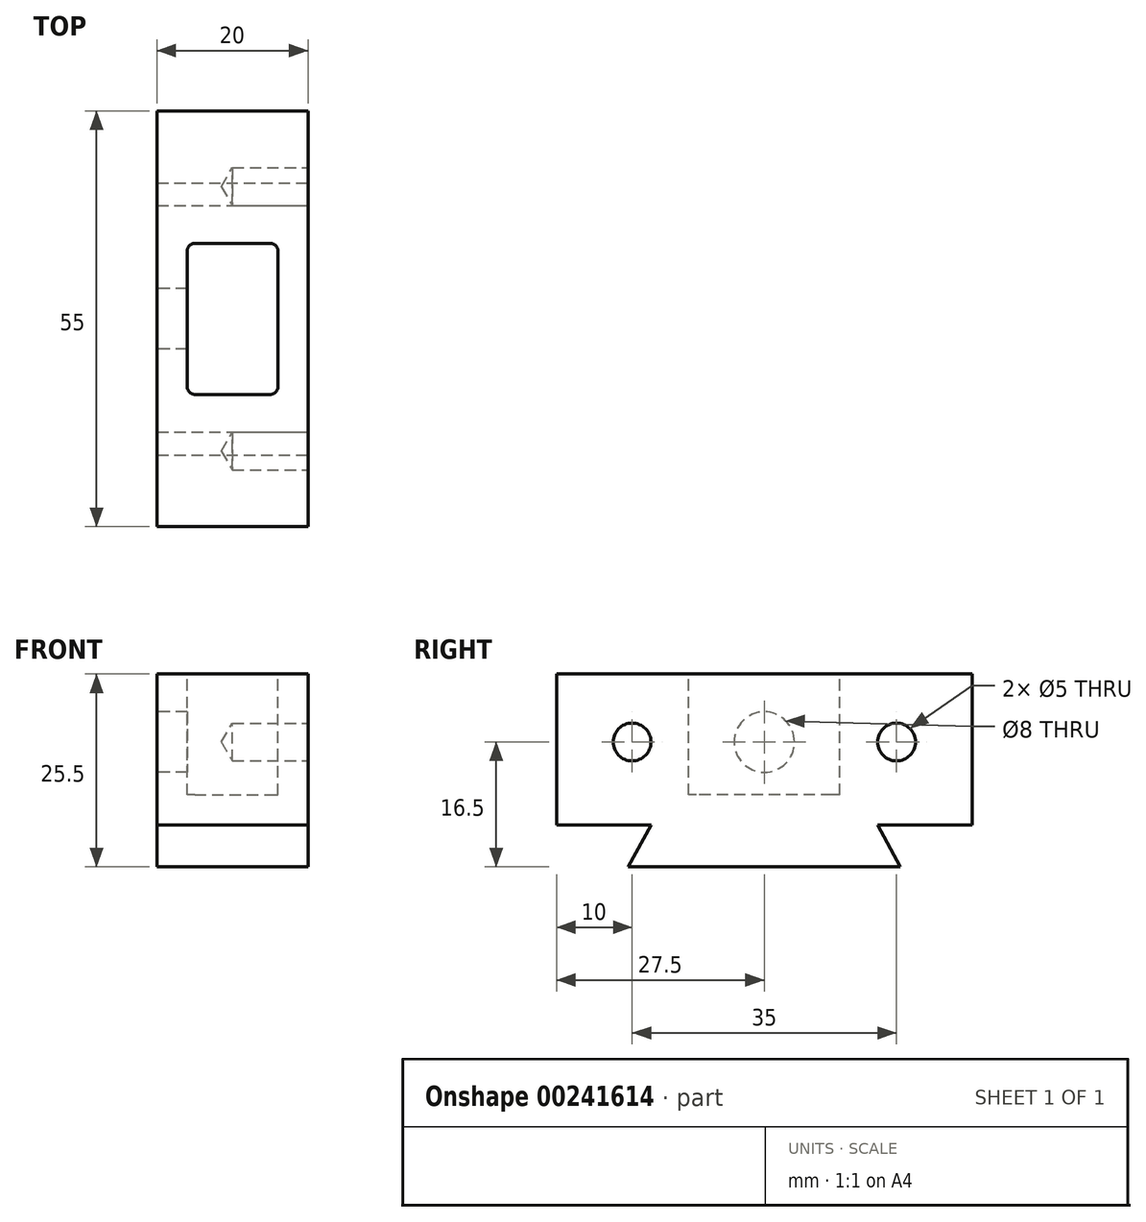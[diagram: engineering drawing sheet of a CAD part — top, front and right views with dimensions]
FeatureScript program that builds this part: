
annotation { "Feature Type Name" : "Feature", "Feature Type Description" : "" }
export const myFeature = defineFeature(function(context is Context, id is Id, definition is map)
    precondition{}
    {
        {
            var Q0;
            Q0=qCreatedBy(makeId("Top.planeOp"),FACE);
            var sketch = newSketch(context, id + "F0", { "sketchPlane" : qUnion([Q0])});
            skLineSegment(sketch, "E0.bottom", {"start": v(10, -27.5) * mm, "end": v(-10, -27.5) * mm});
            skLineSegment(sketch, "E0.top", {"start": v(10, 27.5) * mm, "end": v(-10, 27.5) * mm});
            skLineSegment(sketch, "E0.left", {"start": v(10, -27.5) * mm, "end": v(10, 27.5) * mm});
            skLineSegment(sketch, "E0.right", {"start": v(-10, -27.5) * mm, "end": v(-10, 27.5) * mm});
            skPoint(sketch, "E0.middle", {"position": v(0, 0) * mm});
            skSolve(sketch);
        }
        {
            var Q0;
            Q0 = qSketchRegion(id + "F0", true);
            extrude(context, id + "F1", {"entities" : qUnion([Q0]), "depth" : 25.5 * mm});
        }
        {
            var Q0;
            Q0=makeQuery(id+"F1.opExtrude","CAP_FACE",FACE,{"disambiguationData":[OSD([sQuery(id+"F0.wireOp",EDGE,"E0.bottom"),sQuery(id+"F0.wireOp",EDGE,"E0.top"),sQuery(id+"F0.wireOp",EDGE,"E0.left"),sQuery(id+"F0.wireOp",EDGE,"E0.right")])],"isStart":false});
            var sketch = newSketch(context, id + "F2", { "sketchPlane" : qUnion([Q0])});
            skLineSegment(sketch, "E1.bottom", {"start": v(-5, 10) * mm, "end": v(5, 10) * mm});
            skLineSegment(sketch, "E1.top", {"start": v(-5, -10) * mm, "end": v(5, -10) * mm});
            skLineSegment(sketch, "E1.left", {"start": v(-6, 9) * mm, "end": v(-6, -9) * mm});
            skLineSegment(sketch, "E1.right", {"start": v(6, 9) * mm, "end": v(6, -9) * mm});
            skPoint(sketch, "E1.middle", {"position": v(0, 0) * mm});
            skPoint(sketch, "E2.visualSharp", {"position": v(6, 10) * mm});
            skArc(sketch, "E2.filletArc", {"start": v(6, 9) * mm, "mid": v(5.7, 9.7) * mm, "end": v(5, 10) * mm});
            skPoint(sketch, "E3.visualSharp", {"position": v(-6, 10) * mm});
            skArc(sketch, "E3.filletArc", {"start": v(-5, 10) * mm, "mid": v(-5.7, 9.7) * mm, "end": v(-6, 9) * mm});
            skPoint(sketch, "E4.visualSharp", {"position": v(-6, -10) * mm});
            skArc(sketch, "E4.filletArc", {"start": v(-6, -9) * mm, "mid": v(-5.7, -9.7) * mm, "end": v(-5, -10) * mm});
            skPoint(sketch, "E5.visualSharp", {"position": v(6, -10) * mm});
            skArc(sketch, "E5.filletArc", {"start": v(5, -10) * mm, "mid": v(5.7, -9.7) * mm, "end": v(6, -9) * mm});
            skSolve(sketch);
        }
        {
            var Q0;
            Q0 = qSketchRegion(id + "F2", true);
            extrude(context, id + "F3", {"entities" : qUnion([Q0]), "operationType" : NewBodyOperationType.REMOVE, "oppositeDirection" : true, "depth" : 16 * mm});
        }
        {
            var Q0;
            Q0=makeQuery(id+"F1.opExtrude","SWEPT_FACE",FACE,{"disambiguationData":[OSD([sQuery(id+"F0.wireOp",EDGE,"E0.left")])]});
            var sketch = newSketch(context, id + "F4", { "sketchPlane" : qUnion([Q0])});
            skLineSegment(sketch, "E6", {"start": v(0, 0) * mm, "end": v(0, 25.5) * mm, "construction": true});
            skLineSegment(sketch, "E7", {"start": v(-18, 0) * mm, "end": v(-15, 5.5) * mm});
            skLineSegment(sketch, "E8", {"start": v(-15, 5.5) * mm, "end": v(-27.5, 5.5) * mm});
            skLineSegment(sketch, "E9", {"start": v(-27.5, 5.5) * mm, "end": v(-27.5, 0) * mm});
            skLineSegment(sketch, "E10", {"start": v(-27.5, 0) * mm, "end": v(-18, 0) * mm});
            skLineSegment(sketch, "E11.MirrorCS", {"start": v(15, 5.5) * mm, "end": v(27.5, 5.5) * mm});
            skLineSegment(sketch, "E12.MirrorCS", {"start": v(18, 0) * mm, "end": v(15, 5.5) * mm});
            skLineSegment(sketch, "E13.MirrorCS", {"start": v(27.5, 0) * mm, "end": v(18, 0) * mm});
            skLineSegment(sketch, "E14.MirrorCS", {"start": v(27.5, 5.5) * mm, "end": v(27.5, 0) * mm});
            skSolve(sketch);
        }
        {
            var Q0;
            Q0 = qSketchRegion(id + "F4", true);
            extrude(context, id + "F5", {"entities" : qUnion([Q0]), "operationType" : NewBodyOperationType.REMOVE, "oppositeDirection" : true, "depth" : 25 * mm});
        }
        {
            var Q0;
            Q0=makeQuery(id+"F1.opExtrude","SWEPT_FACE",FACE,{"disambiguationData":[OSD([sQuery(id+"F0.wireOp",EDGE,"E0.left")])]});
            var sketch = newSketch(context, id + "F6", { "sketchPlane" : qUnion([Q0])});
            skPoint(sketch, "E15", {"position": v(-17.5, 16.5) * mm});
            skPoint(sketch, "E16", {"position": v(17.5, 16.5) * mm});
            skSolve(sketch);
        }
        {
            var Q0;
            Q0=sQuery(id+"F6.wireOp",VERTEX,"E15");
            var Q1;
            Q1=sQuery(id+"F6.wireOp",VERTEX,"E16");
            var Q2;
            Q2=makeQuery(id+"F1.opExtrude","SWEPT_BODY",BODY,{"disambiguationData":[OSD([sQuery(id+"F0.wireOp",EDGE,"E0.bottom"),sQuery(id+"F0.wireOp",EDGE,"E0.top"),sQuery(id+"F0.wireOp",EDGE,"E0.left"),sQuery(id+"F0.wireOp",EDGE,"E0.right")])]});
            hole(context, id + "F7", {"style" : HoleStyle.SIMPLE, "endStyle" : HoleEndStyle.BLIND, "holeDiameter" : 5 * mm, "holeDepth" : 10 * mm, "startFromSketch" : true, "locations" : qUnion([Q0, Q1]), "scope" : qUnion([Q2])});
        }
        {
            var Q0;
            Q0=makeQuery(id+"F1.opExtrude","SWEPT_FACE",FACE,{"disambiguationData":[OSD([sQuery(id+"F0.wireOp",EDGE,"E0.right")])]});
            var sketch = newSketch(context, id + "F8", { "sketchPlane" : qUnion([Q0])});
            skPoint(sketch, "E17", {"position": v(0, 16.5) * mm});
            skSolve(sketch);
        }
        {
            var Q0;
            Q0=sQuery(id+"F8.wireOp",VERTEX,"E17");
            var Q1;
            Q1=makeQuery(id+"F1.opExtrude","SWEPT_BODY",BODY,{"disambiguationData":[OSD([sQuery(id+"F0.wireOp",EDGE,"E0.bottom"),sQuery(id+"F0.wireOp",EDGE,"E0.top"),sQuery(id+"F0.wireOp",EDGE,"E0.left"),sQuery(id+"F0.wireOp",EDGE,"E0.right")])]});
            hole(context, id + "F9", {"style" : HoleStyle.SIMPLE, "endStyle" : HoleEndStyle.BLIND, "holeDiameter" : 8 * mm, "holeDepth" : 10 * mm, "startFromSketch" : true, "locations" : qUnion([Q0]), "scope" : qUnion([Q1])});
        }
    });
